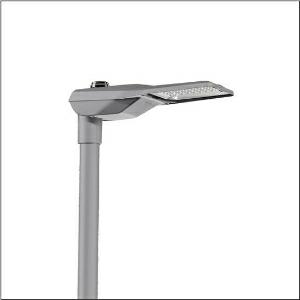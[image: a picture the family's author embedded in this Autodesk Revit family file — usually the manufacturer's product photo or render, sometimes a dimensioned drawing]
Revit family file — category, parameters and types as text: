
# Revit family: streetlight_sl_21_mini___p0_8a_5xe6u67n08gb_cd46
name_source: partatom
category: Lighting Fixtures
units: mm (PartAtom-declared; Revit-internal decimal feet)

## family parameters
Cut with Voids When Loaded = No
Host = Face
Light Source = No
Part Type = Normal
Room Calculation Point = No
Round Connector Dimension = Use Diameter
Shared = No

## types (1)
- --- (1 x LED, 5370 lm, 40.4 W, 2700K)
    Apparent Load = 40 VA
    CIE Flux Codes = 33 69 96 100 100
    Color Rendering = 70
    Color Temperature = 2700K
    Default Elevation = 1800 mm
    Description = Streetlight SL 21 mini, mast luminaire, primary light control with lens, of PMMA, primary optical cover: cover, of toughened safety glass, transparent, light distribution: P0.8a, light emission: direct distribution, primary light characteristic: asymmetric, installation type: side-entry, LED, 3G 1.5mm², High Power LED, rated luminous flux: 5.370lm, luminous efficacy: 133lm/W, light colour: 727, colour temperature: 2700K, control gear: NEMA (7pin), control: flexible luminous flux parameterisation, time-dependent luminous flux control, constant luminous flux control, pre-setting: linear dimming characteristic, overheat protection, mains connection: 230..240V, AC, 50/60Hz, connection cable pre-assembled, cable length: 8,5m, wiring characteristics: H07RN-F, start of lifetime: 40W, end of service life: 41W, reduction: 19W, luminaire housing, of diecast aluminium (EN AC-44300), powder-coated, SITECO metallic grey (DB 702S), corrosivity category C5 high according to DIN EN ISO 12944, multi-level sealing system, sealing non-destructively replaceable, inclination adjustable: 0°, 5°, 10°, 15°, length: 628mm, width: 235mm, height: 110mm, spigot size: 42mm (side-entry), mounting height: 4..8m, protection rating (complete): IP66, insulation class (complete): insulation class I (protective earthing), certification: CE, ENEC, ENEC+, VDE, impact resistance: IK10, permissible operating ambient temperature for outdoor applications: -40..+50°C, standard-compliant lighting for roads and squares, packaging unit: 1 piece

Light Distribution: P0.8a
    Height = 110 mm
    Lamp = 1 x LED
    Lamp Light Flux = 5370 lm
    Lamp Power = 40.4 W
    Lamp count = 1
    Length = 625 mm
    Luminous efficacy = 133 lm/W
    Manufacturer = Siteco
    ModVariant = No
    Model = 5XE6U67N08GB
    Number of Poles = 1
    OnlyDefault = Yes
    Power Factor = 1
    Product Name = Streetlight SL 21 mini | P0.8a
    Product group = mast luminaire | pylon top
    ProductGroupID = 6100
    Protection Class = Protection class I
    Protection Degree = IP 66
    RLX_Detail_Level = 1
    RLX_Emergency_Light_Flux = 0 lm
    RLX_Emergency_Type = 0
    RLX_Emergency_Type_DB = No
    RlxData = <blob elided: 91641 chars, md5=3d312fea>
    Socket = socket
    Standby Power = 0 W
    System Light Flux = 5370 lm
    System Power = 40 W
    Type Comments = factory setting: luminous flux: 100 % | dim-lin: 254 | 812 mA
    Type Image = l_1294379.jpg
    URL = http://relux.com
    VarID = @adj_081167
    Voltage = 0 V
    Weight = 0.00 kg
    Width = 234 mm

## geometry (parser evidence)
native form markers: Blend x4, Sweep x12
no freeform markers — native parametric forms only
